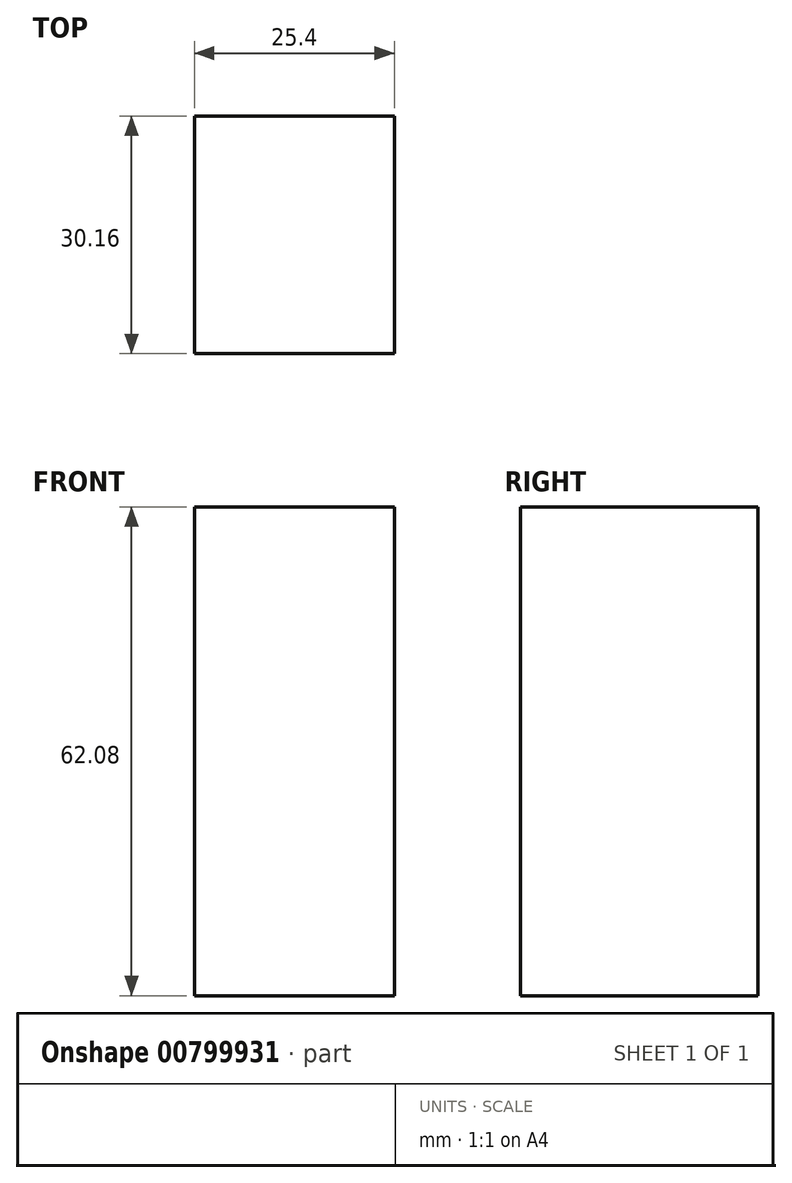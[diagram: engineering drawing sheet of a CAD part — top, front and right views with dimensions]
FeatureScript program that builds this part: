
annotation { "Feature Type Name" : "Feature", "Feature Type Description" : "" }
export const myFeature = defineFeature(function(context is Context, id is Id, definition is map)
    precondition{}
    {
        {
            var Q0;
            Q0=qCreatedBy(makeId("Right.planeOp"),FACE);
            var sketch = newSketch(context, id + "F0", { "sketchPlane" : qUnion([Q0])});
            skLineSegment(sketch, "E0.bottom", {"start": v(11.02, 24.56) * mm, "end": v(41.18, 24.56) * mm});
            skLineSegment(sketch, "E0.top", {"start": v(11.02, -37.52) * mm, "end": v(41.18, -37.52) * mm});
            skLineSegment(sketch, "E0.left", {"start": v(11.02, 24.56) * mm, "end": v(11.02, -37.52) * mm});
            skLineSegment(sketch, "E0.right", {"start": v(41.18, 24.56) * mm, "end": v(41.18, -37.52) * mm});
            skSolve(sketch);
        }
        {
            var Q0;
            Q0=makeQuery(id+"F0.imprint","IMPRINT",FACE,{"disambiguationData":[TD([[makeQuery(id+"F0.imprint","IMPRINT",EDGE,{"derivedFrom":sQuery(id+"F0.wireOp",EDGE,"E0.bottom")}),-1.0]])]});
            extrude(context, id + "F1", {"entities" : qUnion([Q0]), "depth" : 25.4 * mm, "offsetDistance" : 25.4 * mm});
        }
    });
